# Revit family: Access_Door-General_Purpose-Cendrex-Dryall_Flange-(AHD-GYP)
name_source: partatom
category: Specialty Equipment
revit_build: Autodesk Revit Architecture 2013 (Build: 20130531_2115(x64)
units: mm (PartAtom-declared; Revit-internal decimal feet)

## types (10) — shared parameters
Assembly Code = C1020700
Available Options = http://cendrex.com
Cendrex LEED Ready Program = http://www.cendrex.com
Construction Material = Metal - Cendrex - Aluminum
Default Elevation = 0"
Description = General purpose access door with drywall bead flange
Finish = Metal - Cendrex - Powder Coated White
Frame Depth = 1 5/8"
Manufacturer = Cendrex
Max Area = 9 SF
Model = AHD-GYP
Product Documentation Link = http://cendrex.com
Product Page URL = http://cendrex.com
URL = http://www.cendrex.com

## per-type parameters (varying)
| type | Actual Area | Door Height | Door Height Calc | Door Width | Door Width Calc | Height Actual | Width Actual |
| 8 x 8 | 0.44 SF | 8" | 8" | 8" | 8" | 10 19/32" | 10 19/32" |
| 10 x 10 | 0.69 SF | 10" | 10" | 10" | 10" | 12 19/32" | 12 19/32" |
| 12 x 12 | 1 SF | 12" | 12" | 12" | 12" | 14 19/32" | 14 19/32" |
| 14 x 14 | 1.36 SF | 14" | 14" | 14" | 14" | 16 19/32" | 16 19/32" |
| 16 x 16 | 1.78 SF | 16" | 16" | 16" | 16" | 18 19/32" | 18 19/32" |
| 18 x 18 | 2.25 SF | 18" | 18" | 18" | 18" | 20 19/32" | 20 19/32" |
| 22 x 22 | 3.36 SF | 22" | 22" | 22" | 22" | 24 19/32" | 24 19/32" |
| 24 x 24 | 4 SF | 24" | 24" | 24" | 24" | 26 19/32" | 26 19/32" |
| 24 x 36 | 6 SF | 36" | 36" | 24" | 24" | 38 19/32" | 26 19/32" |
| Custom | 4 SF | 24" | 24" | 24" | 24" | 26 19/32" | 26 19/32" |

## geometry (parser evidence)
native form markers: Blend x14, Sweep x21
no freeform markers — native parametric forms only
